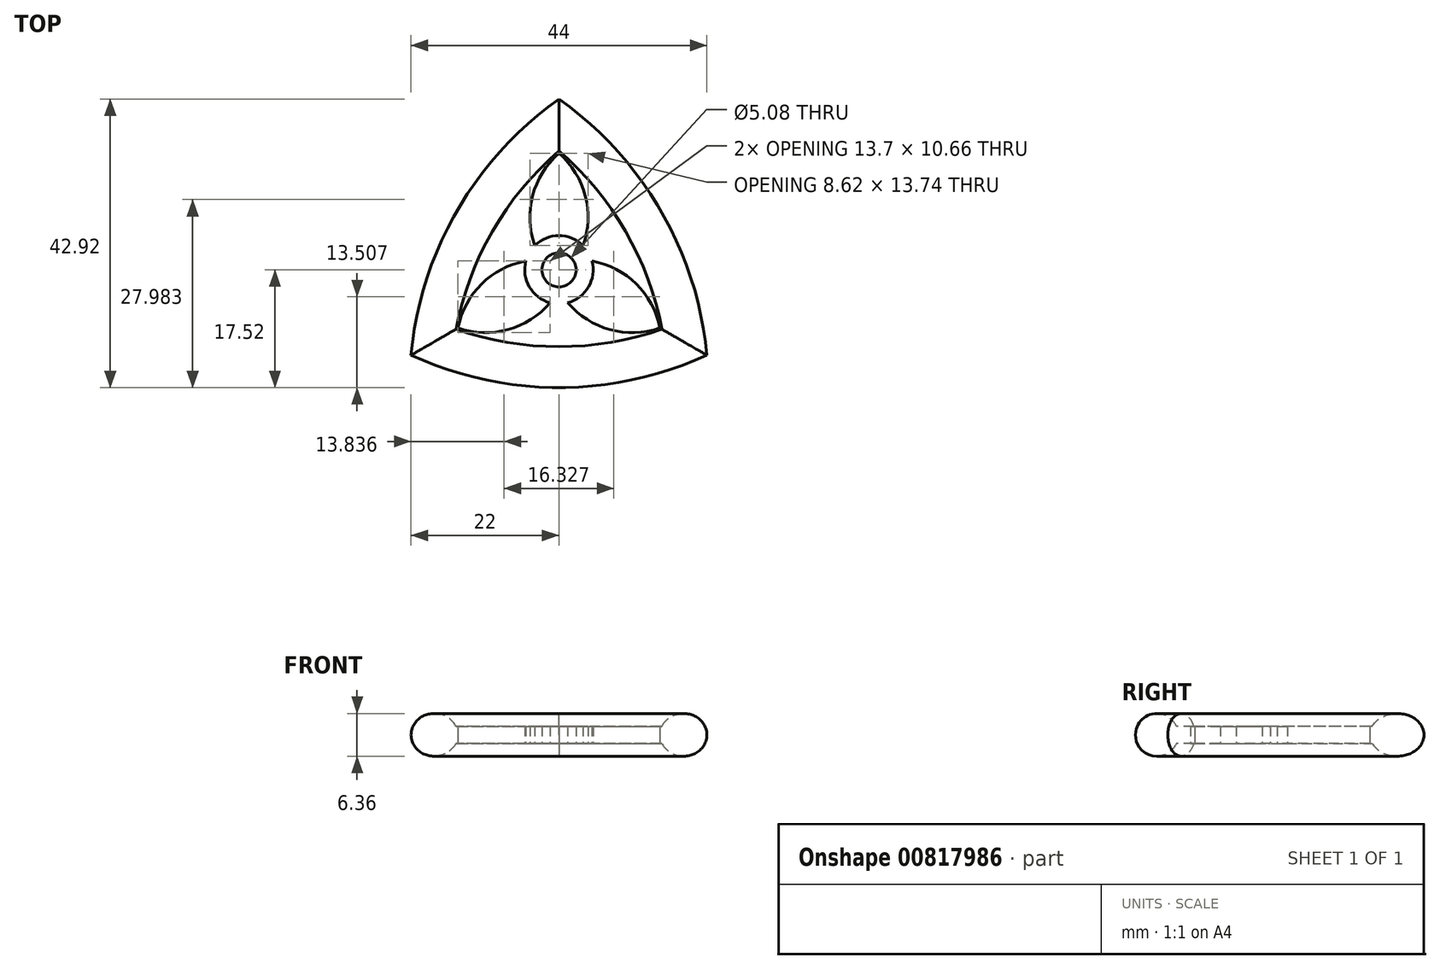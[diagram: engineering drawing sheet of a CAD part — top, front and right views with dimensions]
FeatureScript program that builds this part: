
annotation { "Feature Type Name" : "Feature", "Feature Type Description" : "" }
export const myFeature = defineFeature(function(context is Context, id is Id, definition is map)
    precondition{}
    {
        {
            var Q0;
            Q0=qCreatedBy(makeId("Top.planeOp"),FACE);
            var sketch = newSketch(context, id + "F0", { "sketchPlane" : qUnion([Q0])});
            skCircle(sketch, "E0", {"center": v(0, 0) * mm, "radius": 25.4 * mm, "construction": true});
            skPoint(sketch, "E1", {"position": v(0, 25.4) * mm});
            skPoint(sketch, "E2", {"position": v(-22, -12.7) * mm});
            skPoint(sketch, "E3", {"position": v(22, -12.7) * mm});
            skLineSegment(sketch, "E4", {"start": v(0, 25.4) * mm, "end": v(-22, -12.7) * mm, "construction": true});
            skLineSegment(sketch, "E5", {"start": v(-22, -12.7) * mm, "end": v(22, -12.7) * mm, "construction": true});
            skLineSegment(sketch, "E6", {"start": v(22, -12.7) * mm, "end": v(0, 25.4) * mm, "construction": true});
            skArc(sketch, "E7", {"start": v(0, 25.4) * mm, "mid": v(-15.18, 8.76) * mm, "end": v(-22, -12.7) * mm});
            skArc(sketch, "E8", {"start": v(22, -12.7) * mm, "mid": v(15.18, 8.76) * mm, "end": v(0, 25.4) * mm});
            skArc(sketch, "E9", {"start": v(-22, -12.7) * mm, "mid": v(0, -17.52) * mm, "end": v(22, -12.7) * mm});
            skLineSegment(sketch, "E10", {"start": v(0, 35.05) * mm, "end": v(-30.35, -17.52) * mm, "construction": true});
            skLineSegment(sketch, "E11", {"start": v(-30.35, -17.52) * mm, "end": v(30.35, -17.52) * mm, "construction": true});
            skLineSegment(sketch, "E12", {"start": v(30.35, -17.52) * mm, "end": v(0, 35.05) * mm, "construction": true});
            skArc(sketch, "E13.0", {"start": v(0, 17.33) * mm, "mid": v(-9.68, 5.59) * mm, "end": v(-15.01, -8.67) * mm});
            skArc(sketch, "E13.1", {"start": v(15.01, -8.67) * mm, "mid": v(9.68, 5.59) * mm, "end": v(0, 17.33) * mm});
            skArc(sketch, "E13.2", {"start": v(-15.01, -8.67) * mm, "mid": v(0, -11.17) * mm, "end": v(15.01, -8.67) * mm});
            skPoint(sketch, "E14", {"position": v(0, -11.17) * mm});
            skPoint(sketch, "E15", {"position": v(0, -17.52) * mm});
            skCircle(sketch, "E16", {"center": v(0, 0) * mm, "radius": 2.54 * mm});
            skCircle(sketch, "E17", {"center": v(0, 0) * mm, "radius": 5.08 * mm});
            skArc(sketch, "E18", {"start": v(3.6, 3.6) * mm, "mid": v(3.91, 11.02) * mm, "end": v(0, 17.33) * mm});
            skLineSegment(sketch, "E19", {"start": v(0, 0) * mm, "end": v(3.6, 3.6) * mm, "construction": true});
            skLineSegment(sketch, "E20", {"start": v(-15.01, -8.67) * mm, "end": v(9.68, 5.59) * mm, "construction": true});
            skArc(sketch, "E21.MirrorCS", {"start": v(4.9, 1.31) * mm, "mid": v(11.5, -2.12) * mm, "end": v(15.01, -8.67) * mm});
            skArc(sketch, "E22.MirrorCS", {"start": v(-3.6, 3.6) * mm, "mid": v(-3.91, 11.02) * mm, "end": v(0, 17.33) * mm});
            skArc(sketch, "E23.MirrorCS", {"start": v(-4.9, 1.31) * mm, "mid": v(-11.5, -2.12) * mm, "end": v(-15.01, -8.67) * mm});
            skLineSegment(sketch, "E24", {"start": v(15.01, -8.67) * mm, "end": v(-9.68, 5.59) * mm, "construction": true});
            skLineSegment(sketch, "E25", {"start": v(0, 17.33) * mm, "end": v(0, 0) * mm, "construction": true});
            skArc(sketch, "E26.MirrorCS", {"start": v(1.31, -4.9) * mm, "mid": v(7.58, -8.9) * mm, "end": v(15.01, -8.67) * mm});
            skArc(sketch, "E27.MirrorCS", {"start": v(-1.31, -4.9) * mm, "mid": v(-7.58, -8.9) * mm, "end": v(-15.01, -8.67) * mm});
            skArc(sketch, "E28.0", {"start": v(0, 19) * mm, "mid": v(-10.78, 6.22) * mm, "end": v(-16.46, -9.5) * mm});
            skArc(sketch, "E28.1", {"start": v(16.46, -9.5) * mm, "mid": v(10.78, 6.22) * mm, "end": v(0, 19) * mm});
            skArc(sketch, "E28.2", {"start": v(-16.46, -9.5) * mm, "mid": v(0, -12.44) * mm, "end": v(16.46, -9.5) * mm});
            skSolve(sketch);
        }
        {
            var Q0;
            Q0=makeQuery(id+"F0.imprint","IMPRINT",FACE,{"disambiguationData":[TD([[makeQuery(id+"F0.imprint","IMPRINT",EDGE,{"derivedFrom":sQuery(id+"F0.wireOp",EDGE,"E13.0")}),-1.0]])]});
            var Q1;
            Q1=makeQuery(id+"F0.imprint","IMPRINT",FACE,{"disambiguationData":[TD([[makeQuery(id+"F0.imprint","IMPRINT",EDGE,{"derivedFrom":sQuery(id+"F0.wireOp",EDGE,"E7")}),1.0]])]});
            extrude(context, id + "F1", {"entities" : qUnion([Q0, Q1]), "endBound" : BoundingType.SYMMETRIC, "depth" : 6.35 * mm, "offsetDistance" : 25.4 * mm});
        }
        {
            var Q0;
            Q0=makeQuery(id+"F1.opExtrude","CAP_FACE",FACE,{"disambiguationData":[OSD([sQuery(id+"F0.wireOp",EDGE,"E7"),sQuery(id+"F0.wireOp",EDGE,"E8"),sQuery(id+"F0.wireOp",EDGE,"E9"),sQuery(id+"F0.wireOp",EDGE,"E28.0"),sQuery(id+"F0.wireOp",EDGE,"E28.1"),sQuery(id+"F0.wireOp",EDGE,"E28.2")])],"isStart":false});
            var Q1;
            Q1=makeQuery(id+"F1.opExtrude","CAP_FACE",FACE,{"disambiguationData":[OSD([sQuery(id+"F0.wireOp",EDGE,"E7"),sQuery(id+"F0.wireOp",EDGE,"E8"),sQuery(id+"F0.wireOp",EDGE,"E9"),sQuery(id+"F0.wireOp",EDGE,"E28.0"),sQuery(id+"F0.wireOp",EDGE,"E28.1"),sQuery(id+"F0.wireOp",EDGE,"E28.2")])],"isStart":true});
            fillet(context, id + "F2", {"entities" : qUnion([Q0, Q1]), "radius" : 3.17 * mm, "tangentPropagation" : true, "allowEdgeOverflow" : false});
        }
        {
            var Q0;
            Q0=makeQuery(id+"F0.imprint","IMPRINT",FACE,{"disambiguationData":[TD([[makeQuery(id+"F0.imprint","IMPRINT",EDGE,{"derivedFrom":sQuery(id+"F0.wireOp",EDGE,"E13.0")}),1.0]])]});
            var Q1;
            Q1=makeQuery(id+"F0.imprint","IMPRINT",FACE,{"disambiguationData":[TD([[makeQuery(id+"F0.imprint","IMPRINT",EDGE,{"derivedFrom":sQuery(id+"F0.wireOp",EDGE,"E13.0")}),-1.0]])]});
            var Q2;
            Q2=makeQuery(id+"F0.imprint","IMPRINT",FACE,{"disambiguationData":[TD([[makeQuery(id+"F0.imprint","IMPRINT",EDGE,{"derivedFrom":sQuery(id+"F0.wireOp",EDGE,"E13.1")}),1.0]])]});
            var Q3;
            Q3=makeQuery(id+"F0.imprint","IMPRINT",FACE,{"disambiguationData":[TD([[makeQuery(id+"F0.imprint","IMPRINT",EDGE,{"derivedFrom":sQuery(id+"F0.wireOp",EDGE,"E13.2")}),1.0]])]});
            var Q4;
            Q4=makeQuery(id+"F0.imprint","IMPRINT",FACE,{"disambiguationData":[TD([[makeQuery(id+"F0.imprint","IMPRINT",EDGE,{"derivedFrom":sQuery(id+"F0.wireOp",EDGE,"E16")}),-1.0]])]});
            extrude(context, id + "F3", {"entities" : qUnion([Q0, Q1, Q2, Q3, Q4]), "operationType" : NewBodyOperationType.ADD, "endBound" : BoundingType.SYMMETRIC, "depth" : 2.54 * mm, "offsetDistance" : 25.4 * mm});
        }
    });
